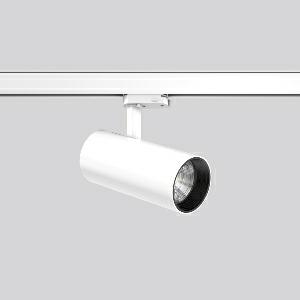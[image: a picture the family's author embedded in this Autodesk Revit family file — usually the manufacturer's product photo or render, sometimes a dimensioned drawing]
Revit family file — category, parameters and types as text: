
# Revit family: deecos_s_mini_742209_002_1_76_5e8d
name_source: partatom
category: Lighting Fixtures
units: mm (PartAtom-declared; Revit-internal decimal feet)

## family parameters
Cut with Voids When Loaded = No
Host = Face
Light Source = No
Part Type = Normal
Room Calculation Point = No
Round Connector Dimension = Use Diameter
Shared = No

## types (1)
- DEECOS S mini (1 x LED Modul 940, 3500 lm, 4000)
    Apparent Load = 29 VA
    Approval mark = CE
    CIE Flux Codes = 80 99 100 100 100
    Color Rendering = 92
    Color Temperature = 4000
    Default Elevation = 1800 mm
    Description = Series: DEECOS S mini
LED surface-mounted projector in modern design with no visible cooling ribs. Housing: die-cast aluminium, powder-coated. Rotation range: 356°. Swivel range: 90°. Black plastic ring and recessed LED to prevent glare from the side. Optical assembly with lens made of plastic (polycarbonate) for the best homogeneous light distribution - can be changed without tools. Best colour rendering index Ra>90. With adapter for RZB 3-circuit DALI tracks. Suitable for Track on ceiling, Wall track. High quality converter without flickering and stroboscopic effect. The following accessories can be mounted without use of tools: interchangeable lenses, decorative glasses, honeycomb louvre, clear and frosted diffusers, white interchangeable plastic ring. 
Colour: traffic white, matt (RAL 9016)
Diameter: 87 mm
Height: 214 mm
Lamp: LED
Socket: without socket
Colour temperature: 4000K
Colour rendering index (CRI): 92
System power: 29 W
Rated luminous flux: 3500 lm
Luminous efficiency: 121 lm/W
Control gear: Converter, dimmable, DALI
Protection class: I
Type of protection: IP 20
    Height = 214 mm
    Lamp = 1 x LED Modul 940
    Lamp Light Flux = 3500 lm
    Lamp count = 1
    Length = 87 mm
    Lifetime = 50000 h
    Luminous efficacy = 121 lm/W
    Manufacturer = RZB
    ModVariant = No
    Model = 742209.002.1.76
    Mounting Place = Ceiling
    Mounting Type = Rail mounted
    Number of Poles = 1
    OnlyDefault = Yes
    Power Factor = 1
    Product Name = DEECOS S mini
    Product group = Track mounted projectors
    ProductGroupID = 301
    Protection Class = Protection class I
    Protection Degree = IP 20
    RLX_Detail_Level = 1
    RLX_Emergency_Light_Flux = 0 lm
    RLX_Emergency_Type = 0
    RLX_Emergency_Type_DB = No
    RlxData = <blob elided: 35701 chars, md5=42ebe446>
    Socket = socket
    Standby Power = 0 W
    System Light Flux = 3500 lm
    System Power = 29 W
    Type Comments = Product without accessories
    Type Image = 741930.002.jpg
    URL = http://relux.com
    VarID = ---
    Voltage = 230 V
    Voltage Range = 220-240 V
    Weight = 0.00 kg
    Width = 0 mm  [stored 0 ft]

note: [stored X ft] marks values corroborated as IEEE doubles in the binary element streams (Revit-internal decimal feet)

## geometry (parser evidence)
native form markers: Blend x4, Sweep x9
no freeform markers — native parametric forms only
